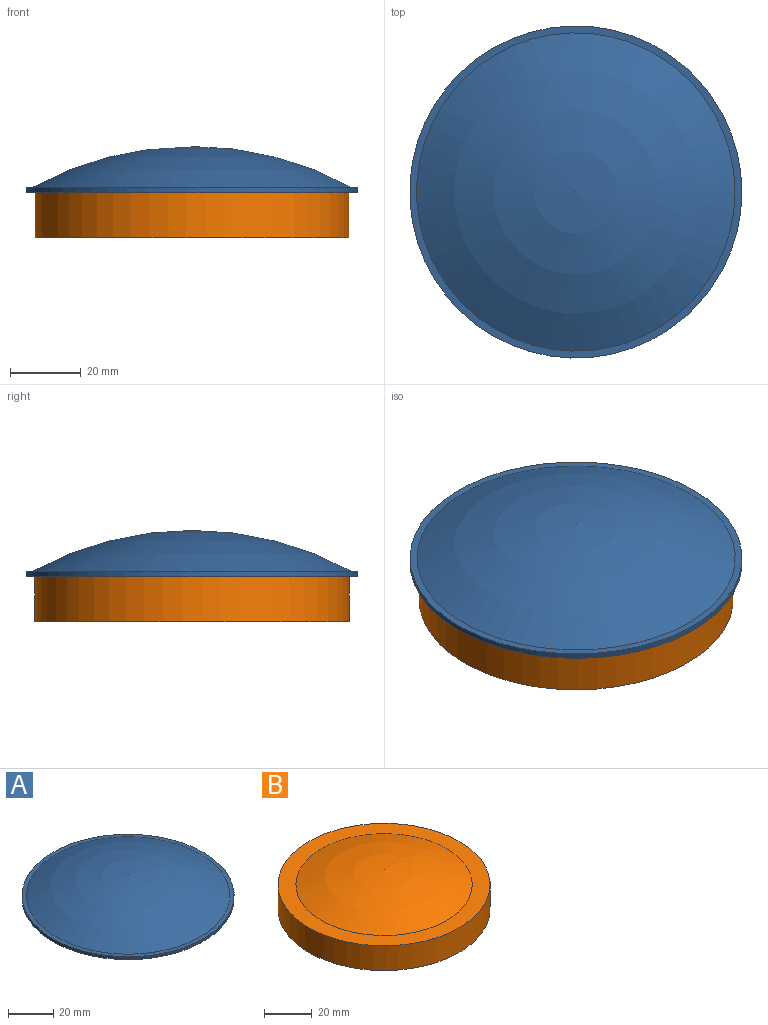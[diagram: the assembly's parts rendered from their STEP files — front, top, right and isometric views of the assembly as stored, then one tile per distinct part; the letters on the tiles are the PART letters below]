
ASSEMBLY  parts=2 mates=1
PART A: 5 faces, bbox 94x94x13.1 mm
  f0: sphere r=93.98mm, area 6786.3mm2, adj f4
  f1: sphere r=93.98mm, area 4476.6mm2, adj f2
  f2: plane 93.98x93.98mm, normal (0,0,-1), area 2640.8mm2, adj f1,f3
  f3: cylinder r=46.99mm len=93.98mm, axis (0,0,1), area 465mm2, adj f2,f4
  f4: plane 93.98x93.98mm, normal (0,0,1), area 565.4mm2, adj f0,f3
PART B: 4 faces, bbox 88.9x88.9x20.3 mm
  f0: plane 88.9x88.9mm, normal (0,0,-1), area 6207.2mm2, adj f1
  f1: cylinder r=44.45mm len=88.9mm, axis (0,0,1), area 3547mm2, adj f0,f2
  f2: plane 88.9x88.9mm, normal (0,0,1), area 1917.6mm2, adj f1,f3
  f3: sphere r=93.98mm, area 4469.6mm2, adj f2
PLACE A t=(-9.35,13.89,22.41)mm
PLACE B t=(-9.35,13.89,9.71)mm
MATE fastened B.f1 <-> A.f3  axis (0,0,1) through (-9.35,13.89,22.41)mm
